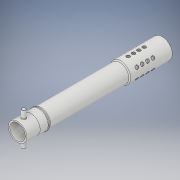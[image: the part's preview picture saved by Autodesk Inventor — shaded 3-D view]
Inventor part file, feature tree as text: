
AUTODESK INVENTOR PART (.ipt)
format: ipt  version: 2019 (Build 230136000, 136)  size: 507,904 bytes
history: native  units: mm
features: other x3, sketch x3, extrude x2, chamfer x2, pattern_circular x2
ambient origin geometry x8: Origin, YZ Plane, XZ Plane, XY Plane, X Axis, Y Axis, Z Axis, Center Point
bodies: Solide1 (feature_tree)
feature tree (12):
  other  "Révolution1"
  other  "Plan de construction1"
  extrude  "Extrusion1"  Depth=24.0mm
  chamfer  "Chanfrein1"  Distance=0.25mm
  pattern_circular  "Réseau circulaire1"  Count=2  [1 undecoded]
  other  "Plan de construction2"
  extrude  "Extrusion2"  Depth=1.0mm
  chamfer  "Chanfrein2"  Distance=1.0mm
  pattern_circular  "Réseau circulaire2"  [2 undecoded]
  sketch  "Esquisse1"
  sketch  "Esquisse2"
  sketch  "Esquisse3"
note: 3 required parameter values undecoded (feature->parameter linkage not recoverable at this tier; creation-order binding heuristic only, values carry confidence <= 0.55)
